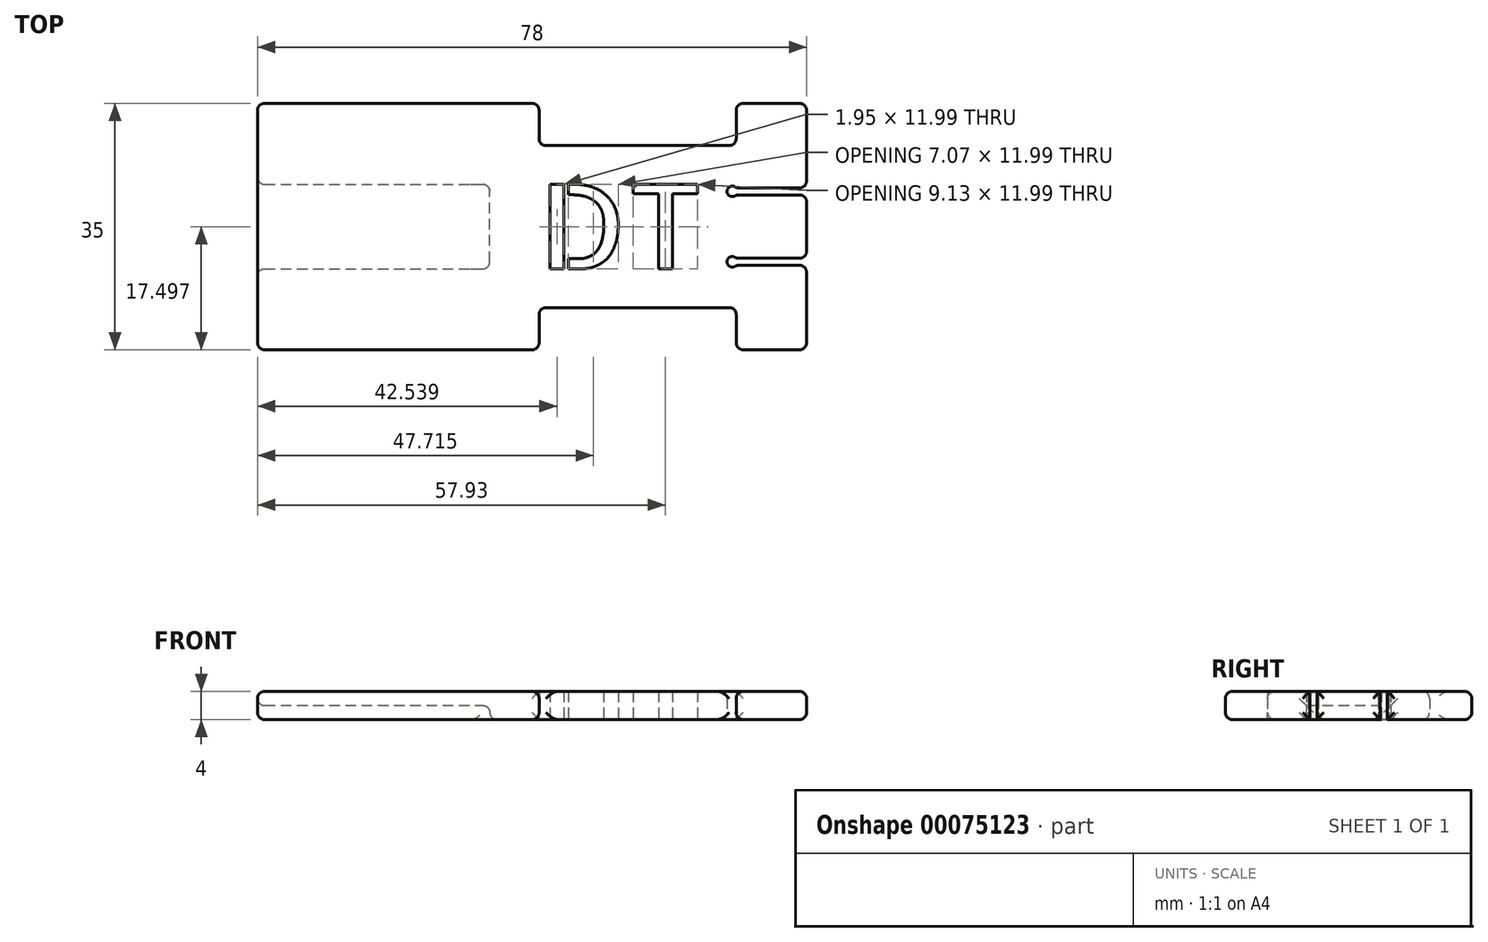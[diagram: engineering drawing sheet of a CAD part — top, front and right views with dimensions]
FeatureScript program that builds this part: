
annotation { "Feature Type Name" : "Feature", "Feature Type Description" : "" }
export const myFeature = defineFeature(function(context is Context, id is Id, definition is map)
    precondition{}
    {
        {
            var Q0;
            Q0=qCreatedBy(makeId("Top.planeOp"),FACE);
            var sketch = newSketch(context, id + "F0", { "sketchPlane" : qUnion([Q0])});
            skLineSegment(sketch, "E0.bottom", {"start": v(28.12, -24.13) * mm, "end": v(18.12, -24.13) * mm});
            skLineSegment(sketch, "E0.top", {"start": v(28.12, 10.87) * mm, "end": v(18.12, 10.87) * mm});
            skLineSegment(sketch, "E0.left", {"start": v(28.12, -24.13) * mm, "end": v(28.12, -12.13) * mm});
            skLineSegment(sketch, "E0.right", {"start": v(-49.88, -24.13) * mm, "end": v(-49.88, 10.87) * mm});
            skPoint(sketch, "E1", {"position": v(-9.88, 10.87) * mm});
            skLineSegment(sketch, "E2.bottom", {"start": v(28.12, -1.13) * mm, "end": v(18.12, -1.13) * mm});
            skLineSegment(sketch, "E2.top", {"start": v(28.12, -2.13) * mm, "end": v(18.12, -2.13) * mm});
            skLineSegment(sketch, "E2.right", {"start": v(18.12, -1.13) * mm, "end": v(18.12, -2.13) * mm});
            skLineSegment(sketch, "E3.bottom", {"start": v(28.12, -11.13) * mm, "end": v(18.12, -11.13) * mm});
            skLineSegment(sketch, "E3.top", {"start": v(28.12, -12.13) * mm, "end": v(18.12, -12.13) * mm});
            skLineSegment(sketch, "E3.right", {"start": v(18.12, -11.13) * mm, "end": v(18.12, -12.13) * mm});
            skArc(sketch, "E4", {"start": v(18.12, -1.13) * mm, "mid": v(16.8, -1.63) * mm, "end": v(18.12, -2.13) * mm});
            skArc(sketch, "E5", {"start": v(18.12, -11.13) * mm, "mid": v(16.8, -11.63) * mm, "end": v(18.12, -12.13) * mm});
            skLineSegment(sketch, "E6", {"start": v(-9.88, 10.87) * mm, "end": v(-9.88, 4.87) * mm});
            skLineSegment(sketch, "E7", {"start": v(-9.88, -24.13) * mm, "end": v(-9.88, -18.13) * mm});
            skLineSegment(sketch, "E8", {"start": v(-9.88, -18.13) * mm, "end": v(18.12, -18.13) * mm});
            skLineSegment(sketch, "E9", {"start": v(18.12, -18.13) * mm, "end": v(18.12, -24.13) * mm});
            skLineSegment(sketch, "E10", {"start": v(-9.88, 4.87) * mm, "end": v(18.12, 4.87) * mm});
            skLineSegment(sketch, "E11", {"start": v(18.12, 4.87) * mm, "end": v(18.12, 10.87) * mm});
            skLineSegment(sketch, "E12.trimOffspring", {"start": v(-9.88, 10.87) * mm, "end": v(-49.88, 10.87) * mm});
            skLineSegment(sketch, "E13.trimOffspring", {"start": v(-9.88, -24.13) * mm, "end": v(-49.88, -24.13) * mm});
            skLineSegment(sketch, "E14.trimOffspring", {"start": v(28.12, -1.13) * mm, "end": v(28.12, 10.87) * mm});
            skLineSegment(sketch, "E15.trimOffspring", {"start": v(28.12, -11.13) * mm, "end": v(28.12, -2.13) * mm});
            skLineSegment(sketch, "E16.bottom", {"start": v(-49.88, -12.63) * mm, "end": v(-16.88, -12.63) * mm});
            skLineSegment(sketch, "E16.top", {"start": v(-49.88, -0.63) * mm, "end": v(-16.88, -0.63) * mm});
            skLineSegment(sketch, "E16.left", {"start": v(-49.88, -12.63) * mm, "end": v(-49.88, -0.63) * mm});
            skLineSegment(sketch, "E16.right", {"start": v(-16.88, -12.63) * mm, "end": v(-16.88, -0.63) * mm});
            skText(sketch, "E17", { "text": "DT", "fontName": "AllertaStencil-Regular.ttf"});
            const initialGuessF0  = {"E17": [-0.00988, -0.01263, 1, 0, 0.012]};
            skSetInitialGuess(sketch, initialGuessF0);
            skSolve(sketch);
        }
        {
            var Q0;
            Q0=makeQuery(id+"F0.imprint","IMPRINT",FACE,{"disambiguationData":[TD([[makeQuery(id+"F0.imprint","IMPRINT",EDGE,{"derivedFrom":sQuery(id+"F0.wireOp",EDGE,"E0.bottom")}),-1.0]])]});
            var Q1;
            Q1=makeQuery(id+"F0.imprint","IMPRINT",FACE,{"disambiguationData":[TD([[makeQuery(id+"F0.imprint","IMPRINT",EDGE,{"derivedFrom":sQuery(id+"F0.wireOp",EDGE,"E16.bottom")}),1.0]])]});
            extrude(context, id + "F1", {"entities" : qUnion([Q0, Q1]), "depth" : 4 * mm});
        }
        {
            var Q0;
            Q0=makeQuery(id+"F0.imprint","IMPRINT",FACE,{"disambiguationData":[TD([[makeQuery(id+"F0.imprint","IMPRINT",EDGE,{"derivedFrom":sQuery(id+"F0.wireOp",EDGE,"E16.bottom")}),1.0]])]});
            extrude(context, id + "F2", {"entities" : qUnion([Q0]), "operationType" : NewBodyOperationType.REMOVE, "depth" : 2 * mm});
        }
        {
            var Q0;
            Q0=makeQuery(id+"F1.opExtrude","SWEPT_FACE",FACE,{"disambiguationData":[OSD([sQuery(id+"F0.wireOp",EDGE,"E7")])]});
            var Q1;
            Q1=makeQuery(id+"F1.opExtrude","SWEPT_FACE",FACE,{"disambiguationData":[OSD([sQuery(id+"F0.wireOp",EDGE,"E9")])]});
            var Q2;
            Q2=makeQuery(id+"F1.opExtrude","SWEPT_FACE",FACE,{"disambiguationData":[OSD([sQuery(id+"F0.wireOp",EDGE,"E13.trimOffspring")])]});
            var Q3;
            Q3=makeQuery(id+"F1.opExtrude","SWEPT_FACE",FACE,{"disambiguationData":[OSD([sQuery(id+"F0.wireOp",EDGE,"E0.right")])]});
            var Q4;
            Q4=makeQuery(id+"F1.opExtrude","SWEPT_FACE",FACE,{"disambiguationData":[OSD([sQuery(id+"F0.wireOp",EDGE,"E12.trimOffspring")])]});
            var Q5;
            Q5=makeQuery(id+"F1.opExtrude","SWEPT_FACE",FACE,{"disambiguationData":[OSD([sQuery(id+"F0.wireOp",EDGE,"E10")])]});
            var Q6;
            Q6=makeQuery(id+"F1.opExtrude","SWEPT_FACE",FACE,{"disambiguationData":[OSD([sQuery(id+"F0.wireOp",EDGE,"E0.top")])]});
            var Q7;
            Q7=makeQuery(id+"F1.opExtrude","SWEPT_FACE",FACE,{"disambiguationData":[OSD([sQuery(id+"F0.wireOp",EDGE,"E14.trimOffspring")])]});
            var Q8;
            Q8=makeQuery(id+"F1.opExtrude","SWEPT_FACE",FACE,{"disambiguationData":[OSD([sQuery(id+"F0.wireOp",EDGE,"E15.trimOffspring")])]});
            var Q9;
            Q9=makeQuery(id+"F1.opExtrude","SWEPT_FACE",FACE,{"disambiguationData":[OSD([sQuery(id+"F0.wireOp",EDGE,"E0.left")])]});
            var Q10;
            Q10=makeQuery(id+"F1.opExtrude","SWEPT_FACE",FACE,{"disambiguationData":[OSD([sQuery(id+"F0.wireOp",EDGE,"E0.bottom")])]});
            var Q11;
            Q11=makeQuery(id+"F2.boolean.opBoolean","COPY",FACE,{"derivedFrom":makeQuery(id+"F2.opExtrude","SWEPT_FACE",FACE,{"disambiguationData":[OSD([sQuery(id+"F0.wireOp",EDGE,"E16.right")])]})});
            fillet(context, id + "F3", {"entities" : qUnion([Q0, Q1, Q2, Q3, Q4, Q5, Q6, Q7, Q8, Q9, Q10, Q11]), "radius" : 1 * mm, "tangentPropagation" : true, "allowEdgeOverflow" : false});
        }
        {
            var Q0;
            Q0=makeQuery(id+"F1.opExtrude","SWEPT_FACE",FACE,{"disambiguationData":[OSD([sQuery(id+"F0.wireOp",EDGE,"E5")])]});
            var Q1;
            Q1=makeQuery(id+"F1.opExtrude","SWEPT_FACE",FACE,{"disambiguationData":[OSD([sQuery(id+"F0.wireOp",EDGE,"E4")])]});
            fillet(context, id + "F4", {"entities" : qUnion([Q0, Q1]), "radius" : 1 * mm, "tangentPropagation" : true, "allowEdgeOverflow" : false});
        }
    });
